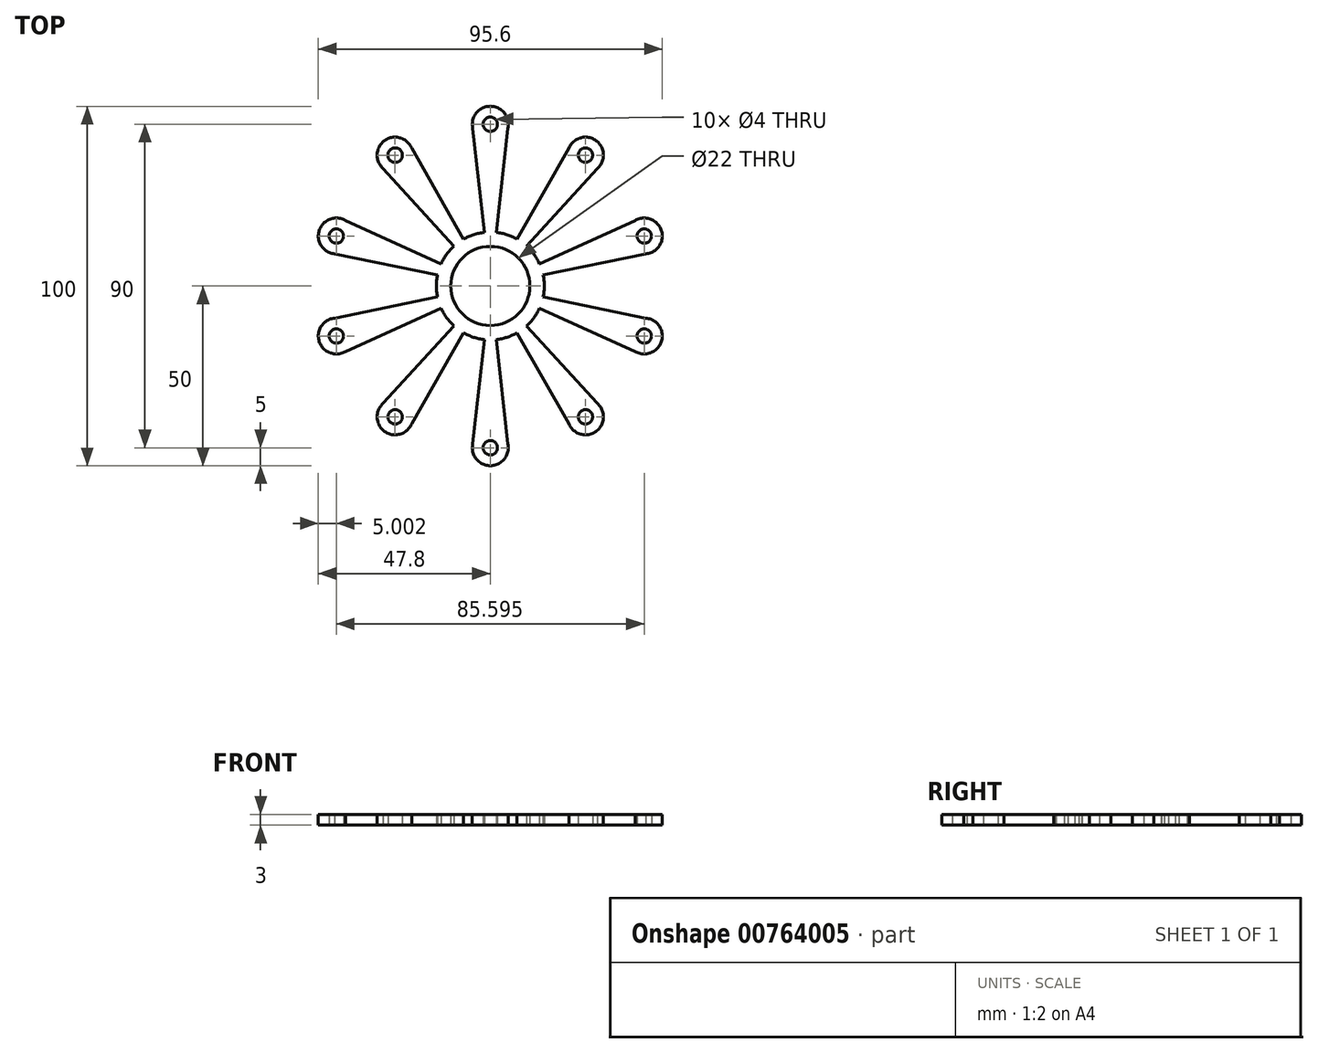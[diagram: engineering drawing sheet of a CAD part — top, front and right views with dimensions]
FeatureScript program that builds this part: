
annotation { "Feature Type Name" : "Feature", "Feature Type Description" : "" }
export const myFeature = defineFeature(function(context is Context, id is Id, definition is map)
    precondition{}
    {
        {
            var Q0;
            Q0=qCreatedBy(makeId("Top.planeOp"),FACE);
            var sketch = newSketch(context, id + "F0", { "sketchPlane" : qUnion([Q0])});
            skArc(sketch, "E0", {"start": v(3.4, 10.46) * mm, "mid": v(0, 11) * mm, "end": v(-3.4, 10.46) * mm});
            skArc(sketch, "E1", {"start": v(4.64, 14.27) * mm, "mid": v(0, 15) * mm, "end": v(-4.64, 14.27) * mm});
            skCircle(sketch, "E2", {"center": v(0, 45) * mm, "radius": 2 * mm});
            skArc(sketch, "E3", {"start": v(4.88, 43.9) * mm, "mid": v(0, 50) * mm, "end": v(-4.88, 43.9) * mm});
            skLineSegment(sketch, "E4", {"start": v(-5, 45) * mm, "end": v(-1.66, 14.9) * mm});
            skLineSegment(sketch, "E5", {"start": v(5, 45) * mm, "end": v(1.66, 14.9) * mm});
            skArc(sketch, "E6.1.0", {"start": v(-21.86, 38.39) * mm, "mid": v(-29.39, 40.45) * mm, "end": v(-29.75, 32.65) * mm});
            skCircle(sketch, "E6.1.1", {"center": v(-26.45, 36.4) * mm, "radius": 2 * mm});
            skLineSegment(sketch, "E6.1.2", {"start": v(-22.4, 39.34) * mm, "end": v(-7.42, 13.03) * mm});
            skLineSegment(sketch, "E6.1.3", {"start": v(-30.5, 33.47) * mm, "end": v(-10.1, 11.09) * mm});
            skArc(sketch, "E6.1.4", {"start": v(-4.64, 14.27) * mm, "mid": v(-8.82, 12.14) * mm, "end": v(-12.14, 8.82) * mm});
            skArc(sketch, "E6.1.7", {"start": v(-3.4, 10.46) * mm, "mid": v(-6.47, 8.9) * mm, "end": v(-8.9, 6.47) * mm});
            skArc(sketch, "E6.2.0", {"start": v(-40.25, 18.2) * mm, "mid": v(-47.55, 15.45) * mm, "end": v(-43.26, 8.93) * mm});
            skCircle(sketch, "E6.2.1", {"center": v(-42.8, 13.9) * mm, "radius": 2 * mm});
            skLineSegment(sketch, "E6.2.2", {"start": v(-41.25, 18.66) * mm, "end": v(-13.67, 6.18) * mm});
            skLineSegment(sketch, "E6.2.3", {"start": v(-44.34, 9.15) * mm, "end": v(-14.7, 3.03) * mm});
            skArc(sketch, "E6.2.4", {"start": v(-12.14, 8.82) * mm, "mid": v(-14.27, 4.64) * mm, "end": v(-15, 0) * mm});
            skArc(sketch, "E6.2.7", {"start": v(-8.9, 6.47) * mm, "mid": v(-10.46, 3.4) * mm, "end": v(-11, 0) * mm});
            skArc(sketch, "E7.3.3.0", {"start": v(-43.26, -8.93) * mm, "mid": v(-47.55, -15.45) * mm, "end": v(-40.25, -18.2) * mm});
            skCircle(sketch, "E7.4.3.0", {"center": v(-42.8, -13.9) * mm, "radius": 2 * mm});
            skLineSegment(sketch, "E7.6.3.0", {"start": v(-44.34, -9.15) * mm, "end": v(-14.7, -3.03) * mm});
            skLineSegment(sketch, "E7.9.3.0", {"start": v(-41.25, -18.66) * mm, "end": v(-13.67, -6.18) * mm});
            skArc(sketch, "E7.12.3.0", {"start": v(-15, 0) * mm, "mid": v(-14.27, -4.64) * mm, "end": v(-12.14, -8.82) * mm});
            skArc(sketch, "E7.22.3.0", {"start": v(-11, 0) * mm, "mid": v(-10.46, -3.4) * mm, "end": v(-8.9, -6.47) * mm});
            skArc(sketch, "E7.3.4.0", {"start": v(-29.75, -32.65) * mm, "mid": v(-29.39, -40.45) * mm, "end": v(-21.86, -38.39) * mm});
            skCircle(sketch, "E7.4.4.0", {"center": v(-26.45, -36.4) * mm, "radius": 2 * mm});
            skLineSegment(sketch, "E7.6.4.0", {"start": v(-30.5, -33.47) * mm, "end": v(-10.1, -11.09) * mm});
            skLineSegment(sketch, "E7.9.4.0", {"start": v(-22.4, -39.34) * mm, "end": v(-7.42, -13.03) * mm});
            skArc(sketch, "E7.12.4.0", {"start": v(-12.14, -8.82) * mm, "mid": v(-8.82, -12.14) * mm, "end": v(-4.64, -14.27) * mm});
            skArc(sketch, "E7.22.4.0", {"start": v(-8.9, -6.47) * mm, "mid": v(-6.47, -8.9) * mm, "end": v(-3.4, -10.46) * mm});
            skArc(sketch, "E7.3.5.0", {"start": v(-4.88, -43.9) * mm, "mid": v(0, -50) * mm, "end": v(4.88, -43.9) * mm});
            skCircle(sketch, "E7.4.5.0", {"center": v(0, -45) * mm, "radius": 2 * mm});
            skLineSegment(sketch, "E7.6.5.0", {"start": v(-5, -45) * mm, "end": v(-1.66, -14.9) * mm});
            skLineSegment(sketch, "E7.9.5.0", {"start": v(5, -45) * mm, "end": v(1.66, -14.9) * mm});
            skArc(sketch, "E7.12.5.0", {"start": v(-4.64, -14.27) * mm, "mid": v(0, -15) * mm, "end": v(4.64, -14.27) * mm});
            skArc(sketch, "E7.22.5.0", {"start": v(-3.4, -10.46) * mm, "mid": v(0, -11) * mm, "end": v(3.4, -10.46) * mm});
            skArc(sketch, "E7.3.6.0", {"start": v(21.86, -38.39) * mm, "mid": v(29.39, -40.45) * mm, "end": v(29.75, -32.65) * mm});
            skCircle(sketch, "E7.4.6.0", {"center": v(26.45, -36.4) * mm, "radius": 2 * mm});
            skLineSegment(sketch, "E7.6.6.0", {"start": v(22.4, -39.34) * mm, "end": v(7.42, -13.03) * mm});
            skLineSegment(sketch, "E7.9.6.0", {"start": v(30.5, -33.47) * mm, "end": v(10.1, -11.09) * mm});
            skArc(sketch, "E7.12.6.0", {"start": v(4.64, -14.27) * mm, "mid": v(8.82, -12.14) * mm, "end": v(12.14, -8.82) * mm});
            skArc(sketch, "E7.22.6.0", {"start": v(3.4, -10.46) * mm, "mid": v(6.47, -8.9) * mm, "end": v(8.9, -6.47) * mm});
            skArc(sketch, "E7.3.7.0", {"start": v(40.25, -18.2) * mm, "mid": v(47.55, -15.45) * mm, "end": v(43.26, -8.93) * mm});
            skCircle(sketch, "E7.4.7.0", {"center": v(42.8, -13.9) * mm, "radius": 2 * mm});
            skLineSegment(sketch, "E7.6.7.0", {"start": v(41.25, -18.66) * mm, "end": v(13.67, -6.18) * mm});
            skLineSegment(sketch, "E7.9.7.0", {"start": v(44.34, -9.15) * mm, "end": v(14.7, -3.03) * mm});
            skArc(sketch, "E7.12.7.0", {"start": v(12.14, -8.82) * mm, "mid": v(14.27, -4.64) * mm, "end": v(15, 0) * mm});
            skArc(sketch, "E7.22.7.0", {"start": v(8.9, -6.47) * mm, "mid": v(10.46, -3.4) * mm, "end": v(11, 0) * mm});
            skArc(sketch, "E7.3.8.0", {"start": v(43.26, 8.93) * mm, "mid": v(47.55, 15.45) * mm, "end": v(40.25, 18.2) * mm});
            skCircle(sketch, "E7.4.8.0", {"center": v(42.8, 13.9) * mm, "radius": 2 * mm});
            skLineSegment(sketch, "E7.6.8.0", {"start": v(44.34, 9.15) * mm, "end": v(14.7, 3.03) * mm});
            skLineSegment(sketch, "E7.9.8.0", {"start": v(41.25, 18.66) * mm, "end": v(13.67, 6.18) * mm});
            skArc(sketch, "E7.12.8.0", {"start": v(15, 0) * mm, "mid": v(14.27, 4.64) * mm, "end": v(12.14, 8.82) * mm});
            skArc(sketch, "E7.22.8.0", {"start": v(11, 0) * mm, "mid": v(10.46, 3.4) * mm, "end": v(8.9, 6.47) * mm});
            skArc(sketch, "E7.3.9.0", {"start": v(29.75, 32.65) * mm, "mid": v(29.39, 40.45) * mm, "end": v(21.86, 38.39) * mm});
            skCircle(sketch, "E7.4.9.0", {"center": v(26.45, 36.4) * mm, "radius": 2 * mm});
            skLineSegment(sketch, "E7.6.9.0", {"start": v(30.5, 33.47) * mm, "end": v(10.1, 11.09) * mm});
            skLineSegment(sketch, "E7.9.9.0", {"start": v(22.4, 39.34) * mm, "end": v(7.42, 13.03) * mm});
            skArc(sketch, "E7.12.9.0", {"start": v(12.14, 8.82) * mm, "mid": v(8.82, 12.14) * mm, "end": v(4.64, 14.27) * mm});
            skArc(sketch, "E7.22.9.0", {"start": v(8.9, 6.47) * mm, "mid": v(6.47, 8.9) * mm, "end": v(3.4, 10.46) * mm});
            skSolve(sketch);
        }
        {
            var Q0;
            Q0 = qSketchRegion(id + "F0", true);
            extrude(context, id + "F1", {"entities" : qUnion([Q0]), "depth" : 3 * mm, "offsetDistance" : 25 * mm});
        }
    });
